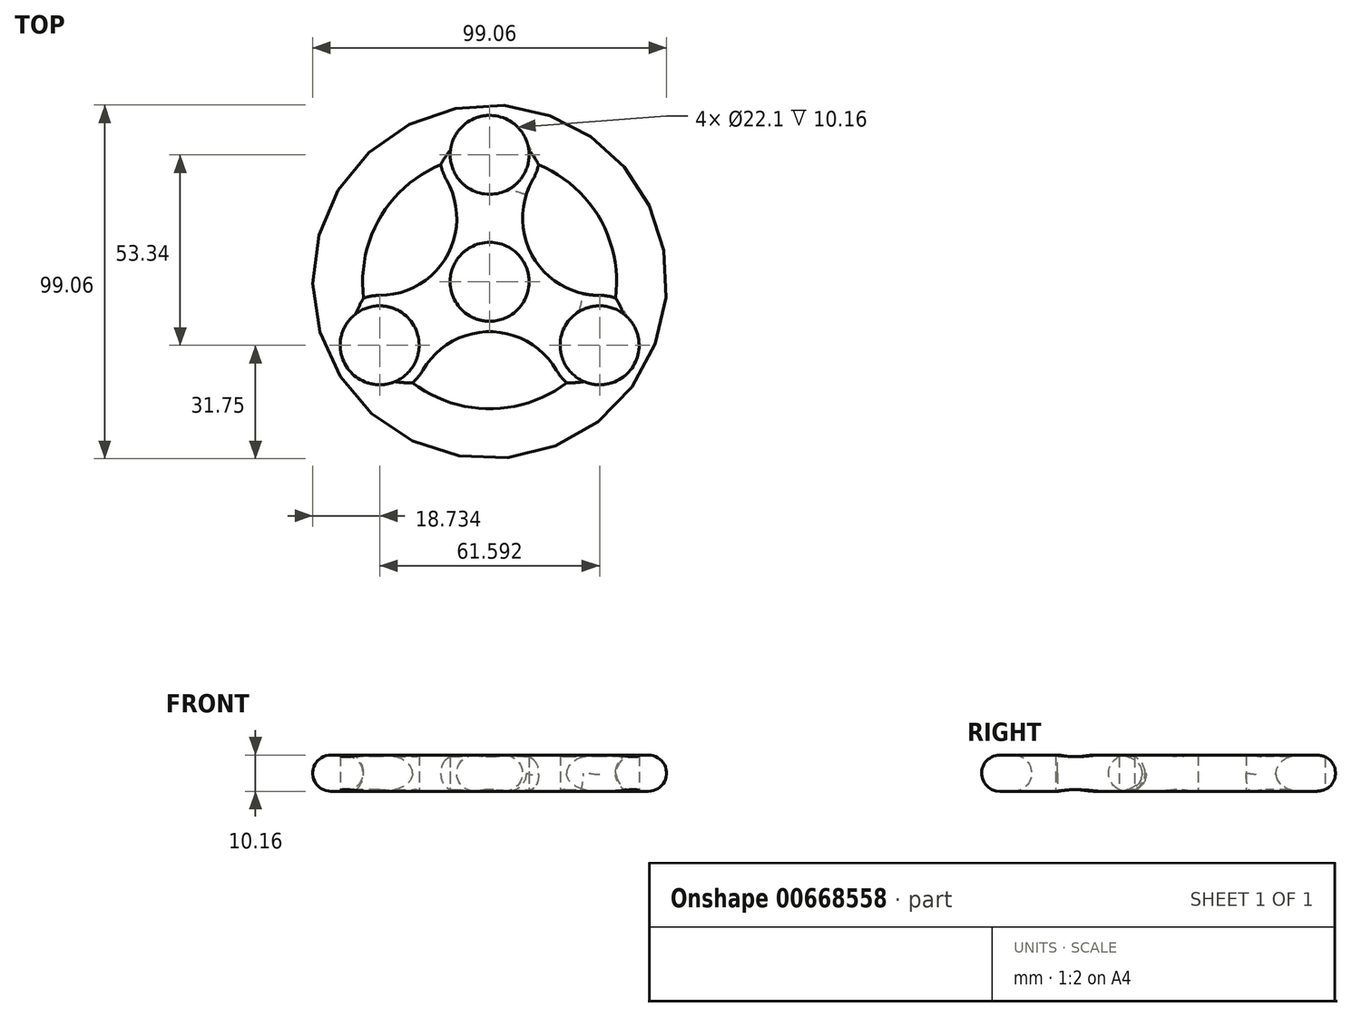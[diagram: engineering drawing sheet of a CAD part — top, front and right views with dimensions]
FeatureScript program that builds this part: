
annotation { "Feature Type Name" : "Feature", "Feature Type Description" : "" }
export const myFeature = defineFeature(function(context is Context, id is Id, definition is map)
    precondition{}
    {
        {
            var Q0;
            Q0=qCreatedBy(makeId("Top.planeOp"),FACE);
            var sketch = newSketch(context, id + "F0", { "sketchPlane" : qUnion([Q0])});
            skCircle(sketch, "E0", {"center": v(0, 0) * mm, "radius": 11.05 * mm});
            skCircle(sketch, "E1", {"center": v(0, 0) * mm, "radius": 13.97 * mm});
            skLineSegment(sketch, "E2", {"start": v(0, 21.59) * mm, "end": v(0, 24.51) * mm});
            skCircle(sketch, "E3", {"center": v(0, 35.56) * mm, "radius": 11.05 * mm});
            skCircle(sketch, "E4", {"center": v(0, 35.56) * mm, "radius": 13.97 * mm});
            skCircle(sketch, "E5.1.0", {"center": v(-30.8, -17.78) * mm, "radius": 13.97 * mm});
            skCircle(sketch, "E5.1.1", {"center": v(-30.8, -17.78) * mm, "radius": 11.05 * mm});
            skCircle(sketch, "E5.2.0", {"center": v(30.8, -17.78) * mm, "radius": 13.97 * mm});
            skCircle(sketch, "E5.2.1", {"center": v(30.8, -17.78) * mm, "radius": 11.05 * mm});
            skArc(sketch, "E6", {"start": v(-30.8, -3.8) * mm, "mid": v(-12.1, 6.99) * mm, "end": v(-12.1, 28.58) * mm});
            skArc(sketch, "E7.1.0", {"start": v(18.7, -24.77) * mm, "mid": v(0, -13.97) * mm, "end": v(-18.7, -24.76) * mm});
            skArc(sketch, "E7.2.0", {"start": v(12.1, 28.57) * mm, "mid": v(12.1, 6.98) * mm, "end": v(30.8, -3.81) * mm});
            skCircle(sketch, "E8", {"center": v(0, 0) * mm, "radius": 49.53 * mm});
            skArc(sketch, "E9", {"start": v(35.27, -4.55) * mm, "mid": v(30.8, 17.78) * mm, "end": v(13.7, 32.82) * mm});
            skArc(sketch, "E10.trimOffspring", {"start": v(-21.57, -28.27) * mm, "mid": v(0, -35.56) * mm, "end": v(21.57, -28.27) * mm});
            skArc(sketch, "E11.trimOffspring", {"start": v(-13.7, 32.82) * mm, "mid": v(-30.8, 17.78) * mm, "end": v(-35.27, -4.55) * mm});
            skSolve(sketch);
        }
        {
            var Q0;
            {var subQ0=sQuery(id+"F0.wireOp",EDGE,"E11.trimOffspring");Q0=makeQuery(id+"F0.imprint","IMPRINT",FACE,{"disambiguationData":[TD([[makeQuery(id+"F0.imprint","IMPRINT",EDGE,{"derivedFrom":subQ0}),-1.0]])]});}
            var Q1;
            {var subQ0=sQuery(id+"F0.wireOp",EDGE,"E9");Q1=makeQuery(id+"F0.imprint","IMPRINT",FACE,{"disambiguationData":[TD([[makeQuery(id+"F0.imprint","IMPRINT",EDGE,{"derivedFrom":subQ0}),-1.0]])]});}
            var Q2;
            Q2=makeQuery(id+"F0.imprint","IMPRINT",FACE,{"disambiguationData":[TD([[makeQuery(id+"F0.imprint","IMPRINT",EDGE,{"derivedFrom":sQuery(id+"F0.wireOp",EDGE,"E3")}),-1.0]])]});
            var Q3;
            {var subQ1=sQuery(id+"F0.wireOp",EDGE,"E4");var subQ5=makeQuery(id+"F0.imprint","IMPRINT",VERTEX,{"derivedFrom":subQ1});Q3=makeQuery(id+"F0.imprint","IMPRINT",FACE,{"disambiguationData":[TD([[makeQuery(id+"F0.imprint","IMPRINT",EDGE,{"disambiguationData":[TD([[subQ5,1.0]])],"derivedFrom":subQ1}),-1.0]])]});}
            var Q4;
            {var subQ0=sQuery(id+"F0.wireOp",EDGE,"E7.2.0");var subQ1=sQuery(id+"F0.wireOp",EDGE,"E1");var subQ2=makeQuery(id+"F0.imprint","INTERSECT",VERTEX,{"derivedFrom":[subQ1,subQ0]});Q4=makeQuery(id+"F0.imprint","IMPRINT",FACE,{"disambiguationData":[TD([[makeQuery(id+"F0.imprint","IMPRINT",EDGE,{"disambiguationData":[TD([[subQ2,1.0]])],"derivedFrom":subQ1}),-1.0]])]});}
            var Q5;
            {var subQ0=sQuery(id+"F0.wireOp",EDGE,"E6");var subQ1=sQuery(id+"F0.wireOp",EDGE,"E1");var subQ2=makeQuery(id+"F0.imprint","INTERSECT",VERTEX,{"derivedFrom":[subQ1,subQ0]});Q5=makeQuery(id+"F0.imprint","IMPRINT",FACE,{"disambiguationData":[TD([[makeQuery(id+"F0.imprint","IMPRINT",EDGE,{"disambiguationData":[TD([[subQ2,-1.0]])],"derivedFrom":subQ1}),-1.0]])]});}
            var Q6;
            Q6=makeQuery(id+"F0.imprint","IMPRINT",FACE,{"disambiguationData":[TD([[makeQuery(id+"F0.imprint","IMPRINT",EDGE,{"derivedFrom":sQuery(id+"F0.wireOp",EDGE,"E0")}),-1.0]])]});
            var Q7;
            Q7=makeQuery(id+"F0.imprint","IMPRINT",FACE,{"disambiguationData":[TD([[makeQuery(id+"F0.imprint","IMPRINT",EDGE,{"derivedFrom":sQuery(id+"F0.wireOp",EDGE,"E5.2.1")}),-1.0]])]});
            var Q8;
            Q8=makeQuery(id+"F0.imprint","IMPRINT",FACE,{"disambiguationData":[TD([[makeQuery(id+"F0.imprint","IMPRINT",EDGE,{"derivedFrom":sQuery(id+"F0.wireOp",EDGE,"E5.1.1")}),-1.0]])]});
            var Q9;
            {var subQ0=sQuery(id+"F0.wireOp",EDGE,"E10.trimOffspring");Q9=makeQuery(id+"F0.imprint","IMPRINT",FACE,{"disambiguationData":[TD([[makeQuery(id+"F0.imprint","IMPRINT",EDGE,{"derivedFrom":subQ0}),-1.0]])]});}
            extrude(context, id + "F1", {"entities" : qUnion([Q0, Q1, Q2, Q3, Q4, Q5, Q6, Q7, Q8, Q9]), "depth" : 10.16 * mm, "offsetDistance" : 25.4 * mm});
        }
        {
            var Q0;
            Q0=makeQuery(id+"F1.opExtrude","CAP_EDGE",EDGE,{"disambiguationData":[OSD([sQuery(id+"F0.wireOp",EDGE,"E8")])],"isStart":false});
            var Q1;
            Q1=makeQuery(id+"F1.opExtrude","CAP_EDGE",EDGE,{"disambiguationData":[OSD([sQuery(id+"F0.wireOp",EDGE,"E7.1.0")])],"isStart":false});
            var Q2;
            Q2=makeQuery(id+"F1.opExtrude","CAP_EDGE",EDGE,{"disambiguationData":[OSD([sQuery(id+"F0.wireOp",EDGE,"E10.trimOffspring")])],"isStart":false});
            var Q3;
            Q3=makeQuery(id+"F1.opExtrude","CAP_EDGE",EDGE,{"disambiguationData":[OSD([sQuery(id+"F0.wireOp",EDGE,"E11.trimOffspring")])],"isStart":false});
            var Q4;
            Q4=makeQuery(id+"F1.opExtrude","CAP_EDGE",EDGE,{"disambiguationData":[OSD([sQuery(id+"F0.wireOp",EDGE,"E6")])],"isStart":false});
            var Q5;
            Q5=makeQuery(id+"F1.opExtrude","CAP_EDGE",EDGE,{"disambiguationData":[OSD([sQuery(id+"F0.wireOp",EDGE,"E7.2.0")])],"isStart":false});
            var Q6;
            Q6=makeQuery(id+"F1.opExtrude","CAP_EDGE",EDGE,{"disambiguationData":[OSD([sQuery(id+"F0.wireOp",EDGE,"E9")])],"isStart":false});
            fillet(context, id + "F2", {"entities" : qUnion([Q0, Q1, Q2, Q3, Q4, Q5, Q6]), "radius" : 5.08 * mm, "tangentPropagation" : true, "allowEdgeOverflow" : false});
        }
        {
            var Q0;
            Q0=makeQuery(id+"F1.opExtrude","CAP_EDGE",EDGE,{"disambiguationData":[OSD([sQuery(id+"F0.wireOp",EDGE,"E8")])],"isStart":true});
            var Q1;
            Q1=makeQuery(id+"F1.opExtrude","CAP_EDGE",EDGE,{"disambiguationData":[OSD([sQuery(id+"F0.wireOp",EDGE,"E10.trimOffspring")])],"isStart":true});
            var Q2;
            Q2=makeQuery(id+"F1.opExtrude","CAP_EDGE",EDGE,{"disambiguationData":[OSD([sQuery(id+"F0.wireOp",EDGE,"E7.1.0")])],"isStart":true});
            var Q3;
            Q3=makeQuery(id+"F1.opExtrude","CAP_EDGE",EDGE,{"disambiguationData":[OSD([sQuery(id+"F0.wireOp",EDGE,"E11.trimOffspring")])],"isStart":true});
            var Q4;
            Q4=makeQuery(id+"F1.opExtrude","CAP_EDGE",EDGE,{"disambiguationData":[OSD([sQuery(id+"F0.wireOp",EDGE,"E6")])],"isStart":true});
            var Q5;
            Q5=makeQuery(id+"F1.opExtrude","CAP_EDGE",EDGE,{"disambiguationData":[OSD([sQuery(id+"F0.wireOp",EDGE,"E9")])],"isStart":true});
            fillet(context, id + "F3", {"entities" : qUnion([Q0, Q1, Q2, Q3, Q4, Q5]), "radius" : 5.08 * mm, "tangentPropagation" : true, "allowEdgeOverflow" : false});
        }
        {
            var Q0;
            Q0=makeQuery(id+"F1.opExtrude","CAP_EDGE",EDGE,{"disambiguationData":[OSD([sQuery(id+"F0.wireOp",EDGE,"E7.2.0")])],"isStart":true});
            fillet(context, id + "F4", {"entities" : qUnion([Q0]), "radius" : 5.08 * mm, "tangentPropagation" : true, "allowEdgeOverflow" : false});
        }
    });
